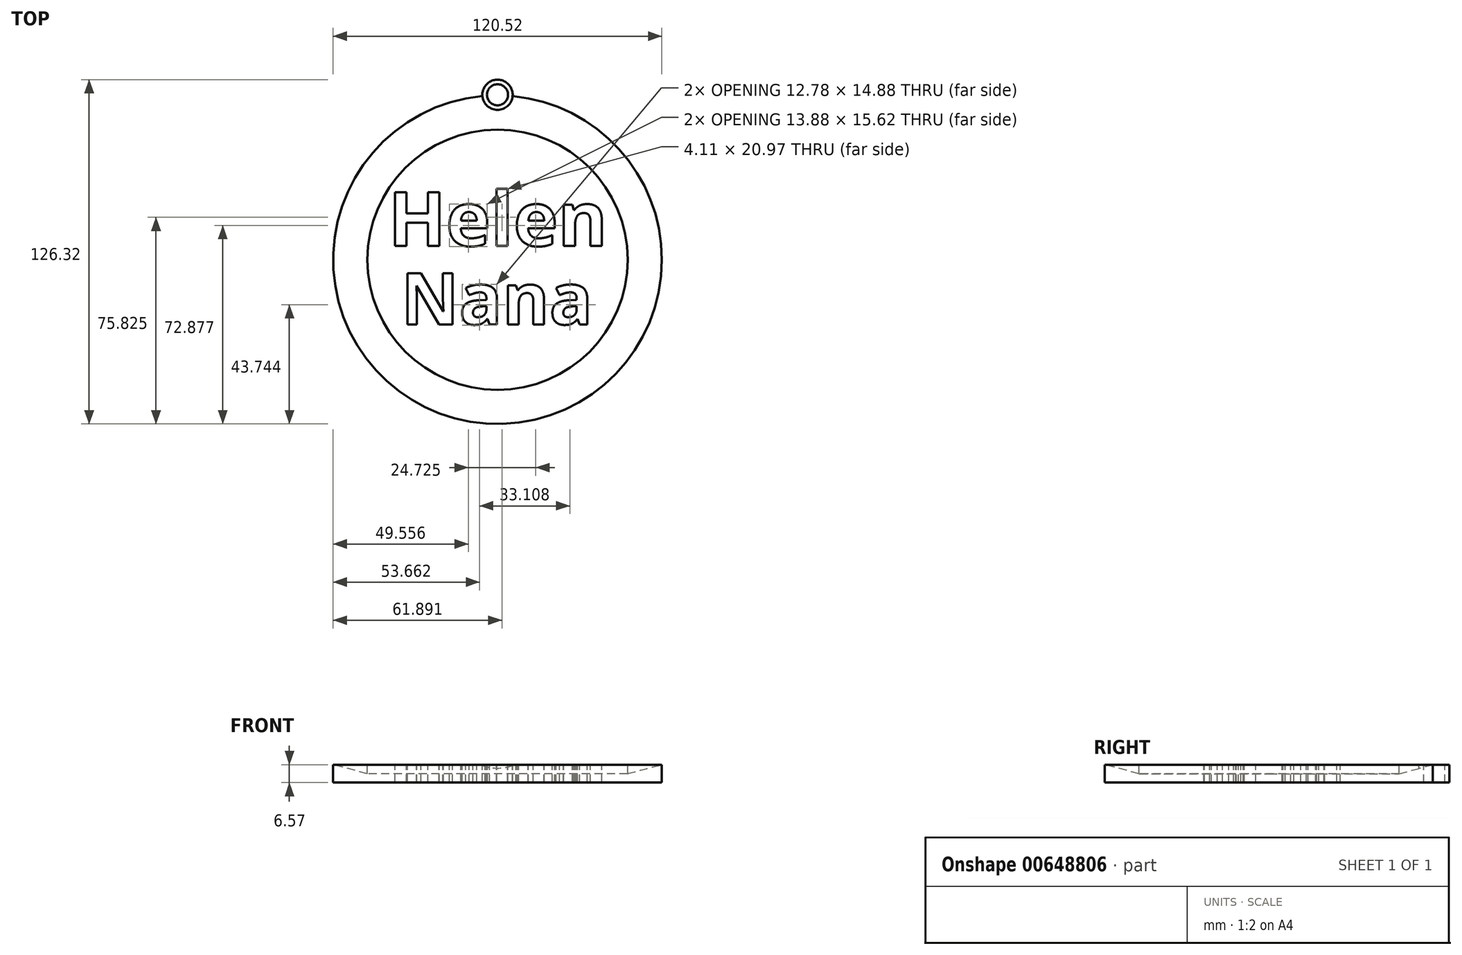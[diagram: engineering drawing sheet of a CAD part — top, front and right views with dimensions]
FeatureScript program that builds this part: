
annotation { "Feature Type Name" : "Feature", "Feature Type Description" : "" }
export const myFeature = defineFeature(function(context is Context, id is Id, definition is map)
    precondition{}
    {
        {
            var Q0;
            Q0=qCreatedBy(makeId("Right.planeOp"),FACE);
            var sketch = newSketch(context, id + "F0", { "sketchPlane" : qUnion([Q0])});
            skLineSegment(sketch, "E0.bottom", {"start": v(0, 0) * mm, "end": v(-47.72, 0) * mm});
            skLineSegment(sketch, "E0.top", {"start": v(0, -6.57) * mm, "end": v(-60.26, -6.57) * mm});
            skLineSegment(sketch, "E0.left", {"start": v(0, 0) * mm, "end": v(0, -6.57) * mm});
            skLineSegment(sketch, "E0.right", {"start": v(-60.26, 0) * mm, "end": v(-60.26, -6.57) * mm});
            skLineSegment(sketch, "E1", {"start": v(-60.26, 0) * mm, "end": v(-47.72, -3.29) * mm});
            skPoint(sketch, "E1.endSnap0", {"position": v(-60.26, -3.29) * mm});
            skLineSegment(sketch, "E2", {"start": v(-47.72, -3.29) * mm, "end": v(-47.72, -6.57) * mm});
            skLineSegment(sketch, "E3", {"start": v(-47.72, -6.57) * mm, "end": v(-47.72, -3.29) * mm});
            skLineSegment(sketch, "E4", {"start": v(-47.72, 0) * mm, "end": v(-47.72, -3.29) * mm});
            skSolve(sketch);
        }
        {
            var Q0;
            Q0 = qSketchRegion(id + "F0", true);
            var Q1;
            Q1=sQuery(id+"F0.wireOp",EDGE,"E0.left");
            revolve(context, id + "F1", {"entities" : qUnion([Q0]), "axis" : qUnion([Q1]), "revolveType" : RevolveType.FULL});
        }
        {
            var Q0;
            Q0=makeQuery(id+"F1.opRevolve","SWEPT_FACE",FACE,{"disambiguationData":[OSD([sQuery(id+"F0.wireOp",EDGE,"E0.bottom")])]});
            var sketch = newSketch(context, id + "F2", { "sketchPlane" : qUnion([Q0])});
            skText(sketch, "E5", { "text": "Helen", "fontName": "OpenSans-Bold.ttf"});
            skText(sketch, "E6", { "text": "Nana", "fontName": "OpenSans-Bold.ttf"});
            const initialGuessF2  = {"E5": [-0.04, 0.00508, 1, 0, 0.01987], "E6": [-0.03543, -0.0237, 1, 0, 0.0189]};
            skSetInitialGuess(sketch, initialGuessF2);
            skSolve(sketch);
        }
        {
            var Q0;
            Q0 = qSketchRegion(id + "F2", true);
            extrude(context, id + "F3", {"entities" : qUnion([Q0]), "operationType" : NewBodyOperationType.REMOVE, "oppositeDirection" : true, "depth" : 101.6 * mm, "offsetDistance" : 25.4 * mm});
        }
        {
            var Q0;
            Q0=qCreatedBy(makeId("Top.planeOp"),FACE);
            var sketch = newSketch(context, id + "F4", { "sketchPlane" : qUnion([Q0])});
            skCircle(sketch, "E7", {"center": v(0, 60.51) * mm, "radius": 5.55 * mm});
            skSolve(sketch);
        }
        {
            var Q0;
            Q0 = qSketchRegion(id + "F4", true);
            extrude(context, id + "F5", {"entities" : qUnion([Q0]), "operationType" : NewBodyOperationType.ADD, "oppositeDirection" : true, "depth" : 6.57 * mm, "offsetDistance" : 25.4 * mm});
        }
        {
            var Q0;
            Q0=makeQuery(id+"F5.opExtrude","CAP_FACE",FACE,{"disambiguationData":[OSD([sQuery(id+"F4.wireOp",EDGE,"E7")])],"isStart":true});
            var sketch = newSketch(context, id + "F6", { "sketchPlane" : qUnion([Q0])});
            skCircle(sketch, "E8", {"center": v(0, 60.51) * mm, "radius": 3.87 * mm});
            skSolve(sketch);
        }
        {
            var Q0;
            Q0 = qSketchRegion(id + "F6", true);
            extrude(context, id + "F7", {"entities" : qUnion([Q0]), "operationType" : NewBodyOperationType.REMOVE, "oppositeDirection" : true, "depth" : 25.4 * mm, "offsetDistance" : 25.4 * mm});
        }
    });
